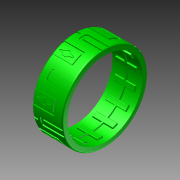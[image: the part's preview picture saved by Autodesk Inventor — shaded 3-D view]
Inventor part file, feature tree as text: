
AUTODESK INVENTOR PART (.ipt)
format: ipt  version: 2015 (Build 190159000, 159)  size: 2,133,504 bytes
history: native  units: in
note: dims shown in document units (in); Inventor stores cm internally (conversion verified against a paired STEP export)
features: fillet x3, sketch x2, revolve x2, pattern_circular x2, plane x1, emboss x1
ambient origin geometry x8: Origin, YZ Plane, XZ Plane, XY Plane, X Axis, Y Axis, Z Axis, Center Point
bodies: Solid1 (feature_tree)
feature tree (11):
  sketch  "Sketch1"  dims[d0=1.65in d1=1.45in]
  revolve  "Revolution1"  [1 undecoded]
  revolve  "Revolution2"  [1 undecoded]
  plane  "Work Plane1"
  fillet  "Fillet1"  Radius=0.3534in
  emboss  "Emboss1"
  fillet  "Fillet2"  Radius=0.05in
  pattern_circular  "Circular Pattern1"  [2 undecoded]
  fillet  "Fillet3"  Radius=0.3in
  pattern_circular  "Circular Pattern2"  [2 undecoded]
  sketch  "Sketch2"  dims[d2=0.58in d3=0.03in d4=0.3534in d5=0.05in d6=0.05in d12=0.3in d15=0.03in d17=0.05in d18=0.2in d25=0.02in d26=0.0in d27=0.05in d28=0.02in d29=0.01in d30=2.7559in d31=360.0deg d33=0.14in d35=0.57in d36=0.08in d37=0.05in d38=0.01in d39=0.13in d40=0.05in d41=0.05in d42=0.4in d43=0.055in d44=0.01in d45=5.9055in d46=360.0deg]
note: 6 required parameter values undecoded (feature->parameter linkage not recoverable at this tier; creation-order binding heuristic only, values carry confidence <= 0.55)